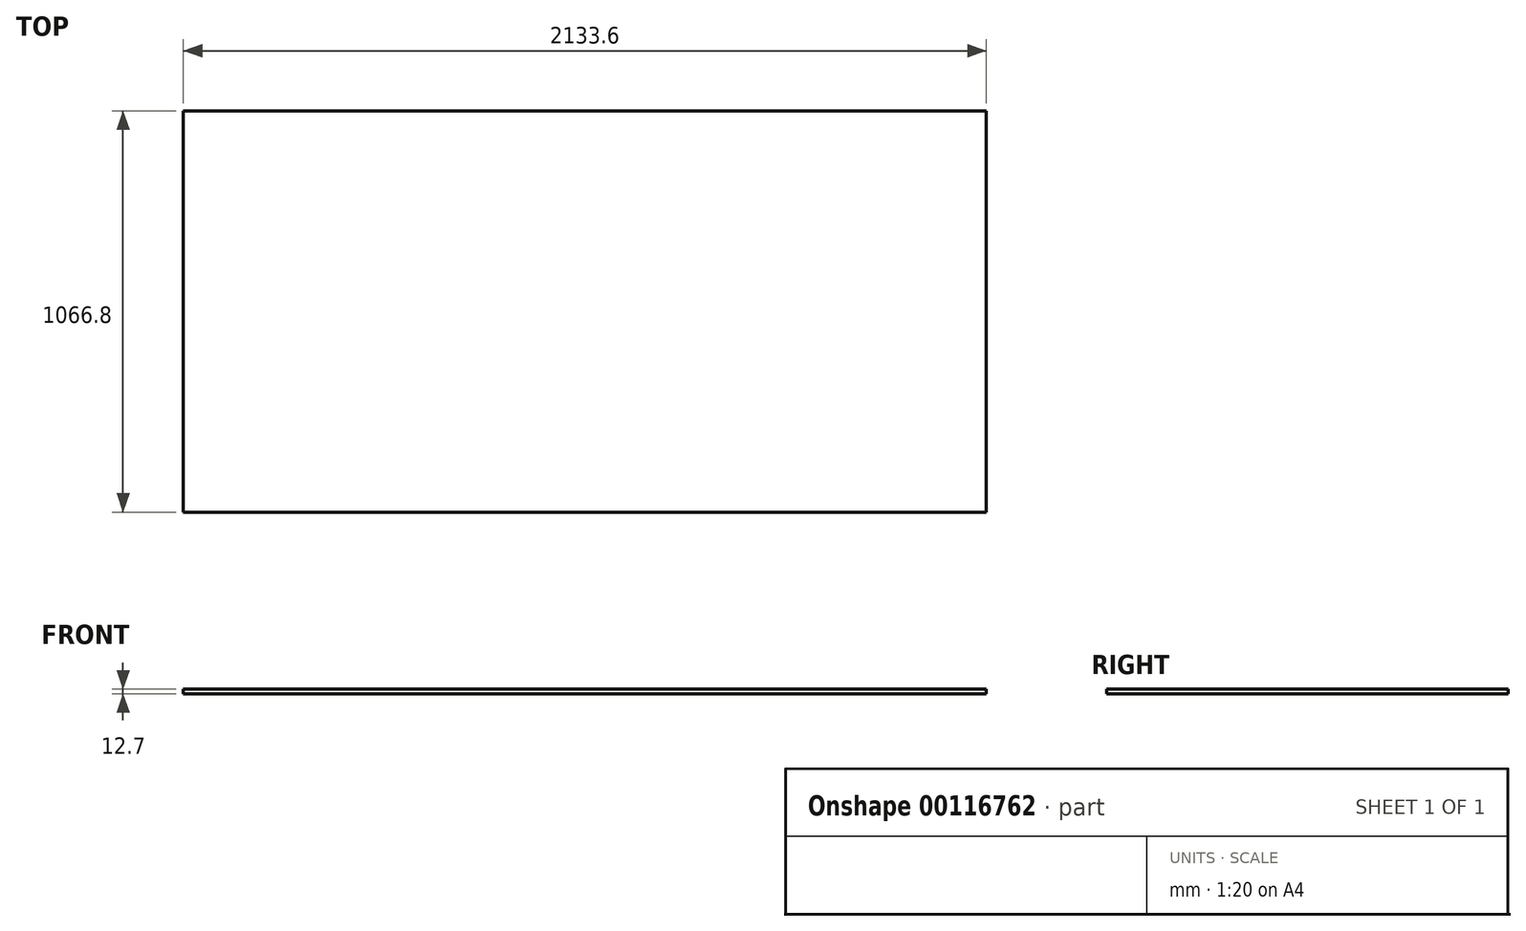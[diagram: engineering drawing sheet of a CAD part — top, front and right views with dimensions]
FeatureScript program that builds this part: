
annotation { "Feature Type Name" : "Feature", "Feature Type Description" : "" }
export const myFeature = defineFeature(function(context is Context, id is Id, definition is map)
    precondition{}
    {
        {
            var Q0;
            Q0=qCreatedBy(makeId("Top.planeOp"),FACE);
            var sketch = newSketch(context, id + "F0", { "sketchPlane" : qUnion([Q0])});
            skLineSegment(sketch, "E0", {"start": v(0, 0) * mm, "end": v(0, 1066.8) * mm});
            skLineSegment(sketch, "E1", {"start": v(0, 1066.8) * mm, "end": v(2133.6, 1066.8) * mm});
            skLineSegment(sketch, "E2", {"start": v(2133.6, 1066.8) * mm, "end": v(2133.6, 0) * mm});
            skLineSegment(sketch, "E3", {"start": v(2133.6, 0) * mm, "end": v(0, 0) * mm});
            skSolve(sketch);
        }
        {
            var Q0;
            Q0=makeQuery(id+"F0.imprint","IMPRINT",FACE,{"disambiguationData":[TD([[makeQuery(id+"F0.imprint","IMPRINT",EDGE,{"derivedFrom":sQuery(id+"F0.wireOp",EDGE,"E0")}),-1.0]])]});
            extrude(context, id + "F1", {"entities" : qUnion([Q0]), "depth" : 12.7 * mm});
        }
    });
